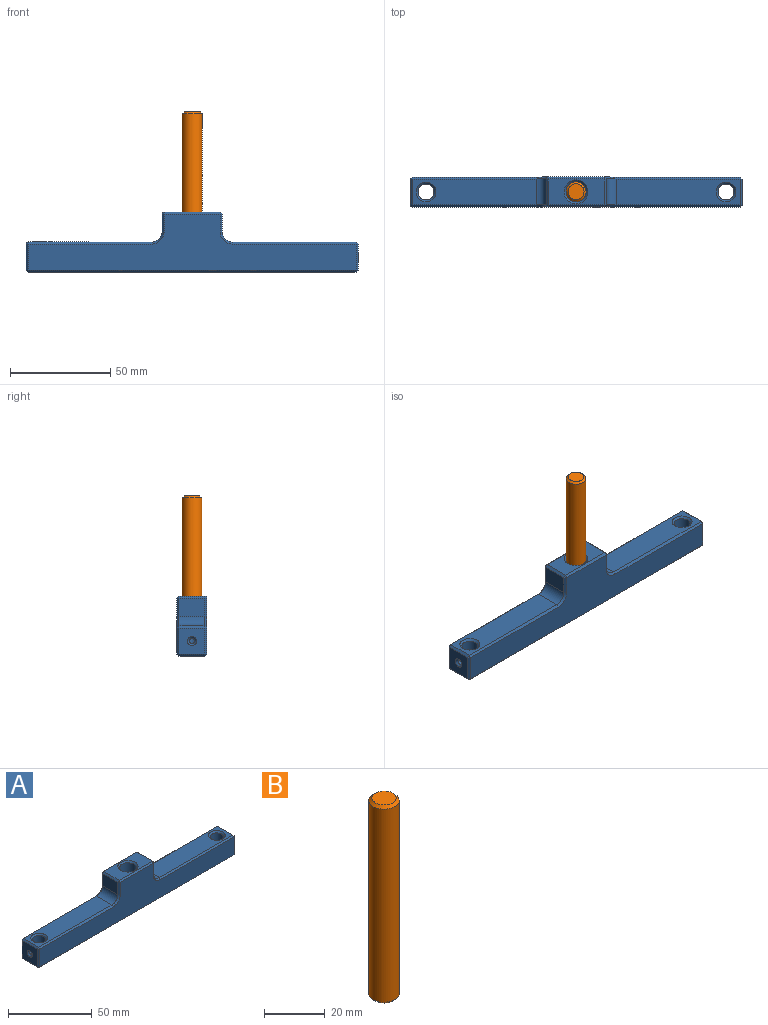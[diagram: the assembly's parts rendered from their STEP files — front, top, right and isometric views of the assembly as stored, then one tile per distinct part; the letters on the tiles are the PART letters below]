
ASSEMBLY  parts=2 mates=1
PART A: 63 faces, bbox 166x15x30 mm
  f0: cylinder r=4mm len=13mm, axis (0,0,-1), area 321.8mm2, adj f14,f19,f61
  f1: cylinder r=4mm len=13mm, axis (0,0,-1), area 321.8mm2, adj f13,f20,f60
  f2: plane 13x13mm, normal (1,0,0), area 153.1mm2, adj f18,f36,f44,f45,f46
  f3: plane 62x13mm, normal (0,0,1), area 727.5mm2, adj f15,f35,f36,f37,f61
  f4: plane 13x9mm, normal (1,0,0), area 117mm2, adj f15,f22,f26,f27
  f5: plane 28x13mm, normal (0,0,1), area 250.9mm2, adj f22,f25,f28,f29,f62
  f6: plane 13x9mm, normal (-1,0,0), area 117mm2, adj f16,f29,f34,f38
  f7: plane 62x13mm, normal (0,0,1), area 727.5mm2, adj f16,f43,f47,f48,f60
  f8: plane 13x13mm, normal (-1,0,0), area 153.1mm2, adj f17,f48,f53,f56,f59
  f9: plane 164x13mm, normal (0,0,-1), area 1861.8mm2, adj f19,f20,f21,f45,f54,f55,f59
  f10: plane 164x28mm, normal (0,-1,0), area 2567.5mm2, adj f25,f26,f31,f34,f35,f39,f43,f44
  f11: plane 164x28mm, normal (0,1,0), area 2567.5mm2, adj f27,f28,f32,f37,f38,f42,f46,f47
  f12: cylinder r=5mm len=28mm, axis (0,0,-1), area 879.6mm2, adj f21,f62
  f13: cylinder r=1.25mm len=3.2mm, axis (-1,0,0), area 24.3mm2, adj f1,f17
  f14: cylinder r=1.25mm len=3.2mm, axis (1,0,0), area 24.3mm2, adj f0,f18
  f15: cylinder r=5mm len=13mm, axis (0,-1,0), area 102.1mm2, adj f3,f4,f31,f32
  f16: cylinder r=5mm len=13mm, axis (0,1,0), area 102.1mm2, adj f6,f7,f39,f42
  f17: cone r=1.25mm half-angle=45deg, axis (-1,0,0), area 15.6mm2, adj f8,f13
  f18: cone r=1.25mm half-angle=45deg, axis (1,0,0), area 15.6mm2, adj f2,f14
  f19: cone r=4mm half-angle=45deg, axis (0,0,-1), area 40mm2, adj f0,f9
  f20: cone r=4mm half-angle=45deg, axis (0,0,-1), area 40mm2, adj f1,f9
  f21: cone r=5mm half-angle=45deg, axis (0,0,-1), area 48.9mm2, adj f9,f12
  f22: plane 13x1mm, normal (0.71,0,0.71), area 18.4mm2, adj f4,f5,f23,f24
  f23: plane 1x1mm, normal (0.58,-0.58,0.58), area 0.9mm2, adj f22,f25,f26
  f24: plane 1x1mm, normal (0.58,0.58,0.58), area 0.9mm2, adj f22,f27,f28
  f25: plane 28x1mm, normal (0,-0.71,0.71), area 39.6mm2, adj f5,f10,f23,f30
  f26: plane 9x1mm, normal (0.71,-0.71,0), area 12.7mm2, adj f4,f10,f23,f31
  f27: plane 9x1mm, normal (0.71,0.71,0), area 12.7mm2, adj f4,f11,f24,f32
  f28: plane 28x1mm, normal (0,0.71,0.71), area 39.6mm2, adj f5,f11,f24,f33
  f29: plane 13x1mm, normal (-0.71,0,0.71), area 18.4mm2, adj f5,f6,f30,f33
  f30: plane 1x1mm, normal (-0.58,-0.58,0.58), area 0.9mm2, adj f25,f29,f34
  f31: cone r=6mm half-angle=45deg, axis (0,-1,0), area 12.2mm2, adj f10,f15,f26,f35
  f32: cone r=6mm half-angle=45deg, axis (0,1,0), area 12.2mm2, adj f11,f15,f27,f37
  f33: plane 1x1mm, normal (-0.58,0.58,0.58), area 0.9mm2, adj f28,f29,f38
  f34: plane 9x1mm, normal (-0.71,-0.71,0), area 12.7mm2, adj f6,f10,f30,f39
  f35: plane 62x1mm, normal (0,-0.71,0.71), area 87.7mm2, adj f3,f10,f31,f40
  f36: plane 13x1mm, normal (0.71,0,0.71), area 18.4mm2, adj f2,f3,f40,f41
  f37: plane 62x1mm, normal (0,0.71,0.71), area 87.7mm2, adj f3,f11,f32,f41
  f38: plane 9x1mm, normal (-0.71,0.71,0), area 12.7mm2, adj f6,f11,f33,f42
  f39: cone r=6mm half-angle=45deg, axis (0,-1,0), area 12.2mm2, adj f10,f16,f34,f43
  f40: plane 1x1mm, normal (0.58,-0.58,0.58), area 0.9mm2, adj f35,f36,f44
  f41: plane 1x1mm, normal (0.58,0.58,0.58), area 0.9mm2, adj f36,f37,f46
  f42: cone r=6mm half-angle=45deg, axis (0,1,0), area 12.2mm2, adj f11,f16,f38,f47
  f43: plane 62x1mm, normal (0,-0.71,0.71), area 87.7mm2, adj f7,f10,f39,f49
  f44: plane 13x1mm, normal (0.71,-0.71,0), area 18.4mm2, adj f2,f10,f40,f50
  f45: plane 13x1mm, normal (0.71,0,-0.71), area 18.4mm2, adj f2,f9,f50,f51
  f46: plane 13x1mm, normal (0.71,0.71,0), area 18.4mm2, adj f2,f11,f41,f51
  f47: plane 62x1mm, normal (0,0.71,0.71), area 87.7mm2, adj f7,f11,f42,f52
  f48: plane 13x1mm, normal (-0.71,0,0.71), area 18.4mm2, adj f7,f8,f49,f52
  f49: plane 1x1mm, normal (-0.58,-0.58,0.58), area 0.9mm2, adj f43,f48,f53
  f50: plane 1x1mm, normal (0.58,-0.58,-0.58), area 0.9mm2, adj f44,f45,f54
  f51: plane 1x1mm, normal (0.58,0.58,-0.58), area 0.9mm2, adj f45,f46,f55
  f52: plane 1x1mm, normal (-0.58,0.58,0.58), area 0.9mm2, adj f47,f48,f56
  f53: plane 13x1mm, normal (-0.71,-0.71,0), area 18.4mm2, adj f8,f10,f49,f57
  f54: plane 164x1mm, normal (0,-0.71,-0.71), area 231.9mm2, adj f9,f10,f50,f57
  f55: plane 164x1mm, normal (0,0.71,-0.71), area 231.9mm2, adj f9,f11,f51,f58
  f56: plane 13x1mm, normal (-0.71,0.71,0), area 18.4mm2, adj f8,f11,f52,f58
  f57: plane 1x1mm, normal (-0.58,-0.58,-0.58), area 0.9mm2, adj f53,f54,f59
  f58: plane 1x1mm, normal (-0.58,0.58,-0.58), area 0.9mm2, adj f55,f56,f59
  f59: plane 13x1mm, normal (-0.71,0,-0.71), area 18.4mm2, adj f8,f9,f57,f58
  f60: cone r=4mm half-angle=45deg, axis (0,0,1), area 40mm2, adj f1,f7
  f61: cone r=4mm half-angle=45deg, axis (0,0,1), area 40mm2, adj f0,f3
  f62: cone r=5mm half-angle=45deg, axis (0,0,1), area 48.9mm2, adj f5,f12
PART B: 5 faces, bbox 10x10x80 mm
  f0: cylinder r=5mm len=78mm, axis (0,0,-1), area 2450.4mm2, adj f3,f4
  f1: plane 8x8mm, normal (0,0,1), area 50.3mm2, adj f4
  f2: plane 8x8mm, normal (0,0,-1), area 50.3mm2, adj f3
  f3: cone r=5mm half-angle=45deg, axis (0,0,1), area 40mm2, adj f0,f2
  f4: cone r=4mm half-angle=45deg, axis (0,0,-1), area 40mm2, adj f0,f1
PLACE A t=(-20.86,-20.17,-1.65)mm
PLACE B t=(-20.86,-20.17,-9.15)mm fixed
MATE fastened A.f21 <-> B.f0  axis (0,0,-1) through (-20.86,-20.17,-9.15)mm
